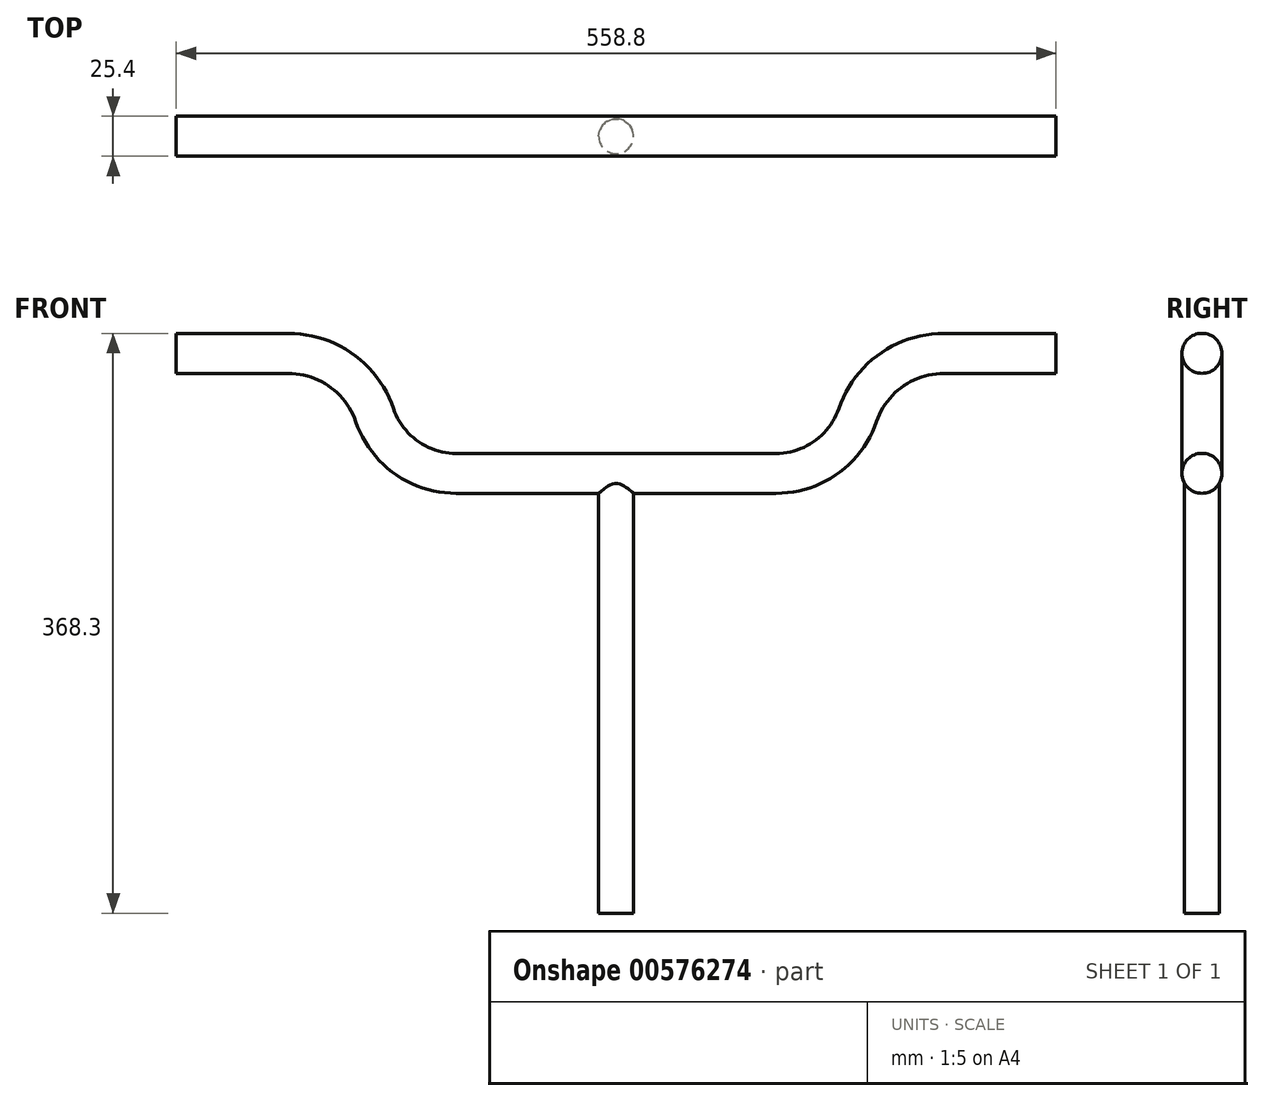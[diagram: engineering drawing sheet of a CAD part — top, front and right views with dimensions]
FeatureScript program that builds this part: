
annotation { "Feature Type Name" : "Feature", "Feature Type Description" : "" }
export const myFeature = defineFeature(function(context is Context, id is Id, definition is map)
    precondition{}
    {
        {
            var Q0;
            Q0=qCreatedBy(makeId("Front.planeOp"),FACE);
            var sketch = newSketch(context, id + "F0", { "sketchPlane" : qUnion([Q0])});
            skLineSegment(sketch, "E0", {"start": v(0, 12.7) * mm, "end": v(0, -12.7) * mm, "construction": true});
            skLineSegment(sketch, "E1", {"start": v(0, 12.7) * mm, "end": v(-101.6, 12.7) * mm});
            skLineSegment(sketch, "E2", {"start": v(0, -12.7) * mm, "end": v(-101.6, -12.7) * mm});
            skArc(sketch, "E3", {"start": v(-165.42, 32.93) * mm, "mid": v(-140.83, -0.12) * mm, "end": v(-101.6, -12.7) * mm});
            skArc(sketch, "E4", {"start": v(-141.38, 41.14) * mm, "mid": v(-126.05, 20.54) * mm, "end": v(-101.6, 12.7) * mm});
            skArc(sketch, "E5", {"start": v(-165.42, 32.93) * mm, "mid": v(-181.9, 55.07) * mm, "end": v(-208.18, 63.5) * mm});
            skArc(sketch, "E6", {"start": v(-141.38, 41.14) * mm, "mid": v(-167.12, 75.73) * mm, "end": v(-208.18, 88.9) * mm});
            skLineSegment(sketch, "E7", {"start": v(-208.18, 88.9) * mm, "end": v(-279.4, 88.9) * mm});
            skLineSegment(sketch, "E8", {"start": v(-279.4, 63.5) * mm, "end": v(-279.4, 88.9) * mm});
            skLineSegment(sketch, "E9", {"start": v(-279.4, 63.5) * mm, "end": v(-208.18, 63.5) * mm});
            skArc(sketch, "E10.MirrorCS", {"start": v(165.42, 32.93) * mm, "mid": v(181.9, 55.07) * mm, "end": v(208.18, 63.5) * mm});
            skArc(sketch, "E11.MirrorCS", {"start": v(141.38, 41.14) * mm, "mid": v(167.12, 75.73) * mm, "end": v(208.18, 88.9) * mm});
            skArc(sketch, "E12.MirrorCS", {"start": v(141.38, 41.14) * mm, "mid": v(126.05, 20.54) * mm, "end": v(101.6, 12.7) * mm});
            skLineSegment(sketch, "E13.MirrorCS", {"start": v(279.4, 63.5) * mm, "end": v(279.4, 88.9) * mm});
            skLineSegment(sketch, "E14.MirrorCS", {"start": v(208.18, 88.9) * mm, "end": v(279.4, 88.9) * mm});
            skLineSegment(sketch, "E15.MirrorCS", {"start": v(0, 12.7) * mm, "end": v(101.6, 12.7) * mm});
            skLineSegment(sketch, "E16.MirrorCS", {"start": v(0, -12.7) * mm, "end": v(101.6, -12.7) * mm});
            skArc(sketch, "E17.MirrorCS", {"start": v(165.42, 32.93) * mm, "mid": v(140.83, -0.12) * mm, "end": v(101.6, -12.7) * mm});
            skLineSegment(sketch, "E18.MirrorCS", {"start": v(279.4, 63.5) * mm, "end": v(208.18, 63.5) * mm});
            skSolve(sketch);
        }
        {
            var Q0;
            Q0=makeQuery(id+"F0.imprint","IMPRINT",FACE,{"disambiguationData":[TD([[makeQuery(id+"F0.imprint","IMPRINT",EDGE,{"derivedFrom":sQuery(id+"F0.wireOp",EDGE,"E1")}),1.0]])]});
            extrude(context, id + "F1", {"entities" : qUnion([Q0]), "depth" : 25.4 * mm, "offsetDistance" : 25.4 * mm});
        }
        {
            var Q0;
            Q0=makeQuery(id+"F1.opExtrude","CAP_EDGE",EDGE,{"disambiguationData":[OSD([sQuery(id+"F0.wireOp",EDGE,"E9")])],"isStart":false});
            var Q1;
            Q1=makeQuery(id+"F1.opExtrude","CAP_EDGE",EDGE,{"disambiguationData":[OSD([sQuery(id+"F0.wireOp",EDGE,"E4")])],"isStart":false});
            var Q2;
            Q2=makeQuery(id+"F1.opExtrude","CAP_EDGE",EDGE,{"disambiguationData":[OSD([sQuery(id+"F0.wireOp",EDGE,"E7")])],"isStart":true});
            var Q3;
            Q3=makeQuery(id+"F1.opExtrude","CAP_EDGE",EDGE,{"disambiguationData":[OSD([sQuery(id+"F0.wireOp",EDGE,"E9")])],"isStart":true});
            fillet(context, id + "F2", {"entities" : qUnion([Q0, Q1, Q2, Q3]), "radius" : 12.7 * mm, "tangentPropagation" : true, "allowEdgeOverflow" : false});
        }
        {
            var Q0;
            Q0=qCreatedBy(makeId("Top.planeOp"),FACE);
            var sketch = newSketch(context, id + "F3", { "sketchPlane" : qUnion([Q0])});
            skCircle(sketch, "E19", {"center": v(0, -12.7) * mm, "radius": 12.7 * mm, "construction": true});
            skCircle(sketch, "E20", {"center": v(0, -12.7) * mm, "radius": 11.05 * mm});
            skSolve(sketch);
        }
        {
            var Q0;
            Q0 = qSketchRegion(id + "F3", true);
            extrude(context, id + "F4", {"entities" : qUnion([Q0]), "operationType" : NewBodyOperationType.ADD, "oppositeDirection" : true, "depth" : 279.4 * mm, "offsetDistance" : 25.4 * mm});
        }
    });
